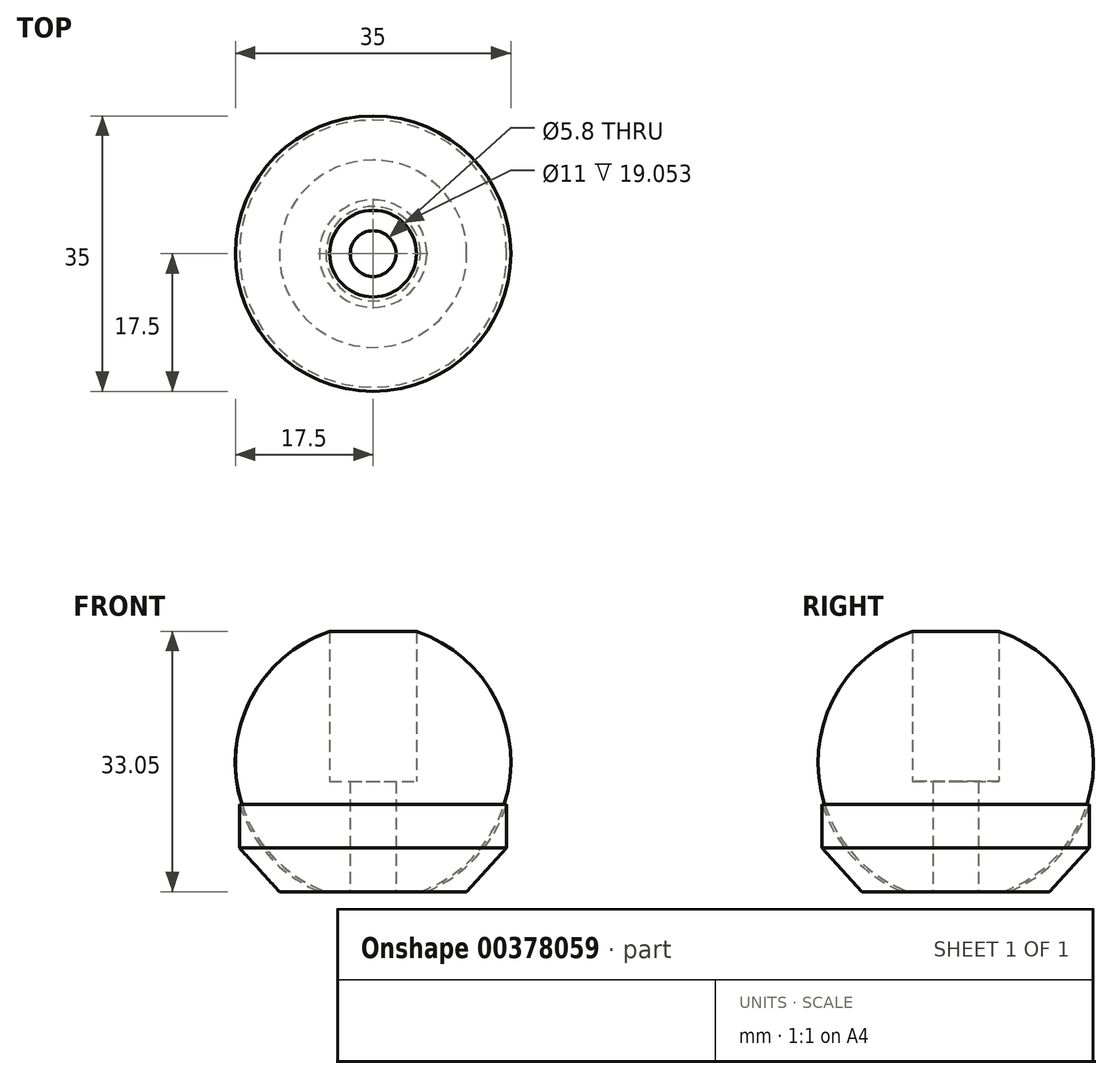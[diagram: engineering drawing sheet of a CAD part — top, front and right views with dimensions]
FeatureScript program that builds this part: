
annotation { "Feature Type Name" : "Feature", "Feature Type Description" : "" }
export const myFeature = defineFeature(function(context is Context, id is Id, definition is map)
    precondition{}
    {
        {
            var Q0;
            Q0=qCreatedBy(makeId("Front.planeOp"),FACE);
            var sketch = newSketch(context, id + "F0", { "sketchPlane" : qUnion([Q0])});
            skLineSegment(sketch, "E0", {"start": v(2.9, 0.82) * mm, "end": v(2.9, 14.82) * mm});
            skLineSegment(sketch, "E1", {"start": v(2.9, 14.82) * mm, "end": v(5.5, 14.82) * mm});
            skLineSegment(sketch, "E2", {"start": v(5.5, 14.82) * mm, "end": v(5.5, 33.87) * mm});
            skArc(sketch, "E3", {"start": v(6, 0.82) * mm, "mid": v(17.5, 17.52) * mm, "end": v(5.5, 33.87) * mm});
            skLineSegment(sketch, "E4", {"start": v(0, 0) * mm, "end": v(0, 22.12) * mm, "construction": true});
            skLineSegment(sketch, "E5", {"start": v(2.9, 0.82) * mm, "end": v(6, 0.82) * mm});
            skPoint(sketch, "E6.orphan", {"position": v(2.9, 0) * mm});
            skLineSegment(sketch, "E7", {"start": v(6.83, 0.82) * mm, "end": v(11.9, 0.82) * mm});
            skLineSegment(sketch, "E8", {"start": v(16.97, 6.36) * mm, "end": v(16.97, 11.9) * mm});
            skArc(sketch, "E9", {"start": v(6.83, 0.82) * mm, "mid": v(13.13, 5.23) * mm, "end": v(16.97, 11.9) * mm});
            skLineSegment(sketch, "E10", {"start": v(11.9, 0.82) * mm, "end": v(16.97, 6.36) * mm});
            skPoint(sketch, "E11.orphan", {"position": v(16.97, 0.82) * mm});
            skSolve(sketch);
        }
        {
            var Q0;
            Q0 = qSketchRegion(id + "F0", true);
            var Q1;
            Q1=sQuery(id+"F0.wireOp",EDGE,"E4");
            revolve(context, id + "F1", {"entities" : qUnion([Q0]), "axis" : qUnion([Q1]), "revolveType" : RevolveType.FULL});
        }
    });
